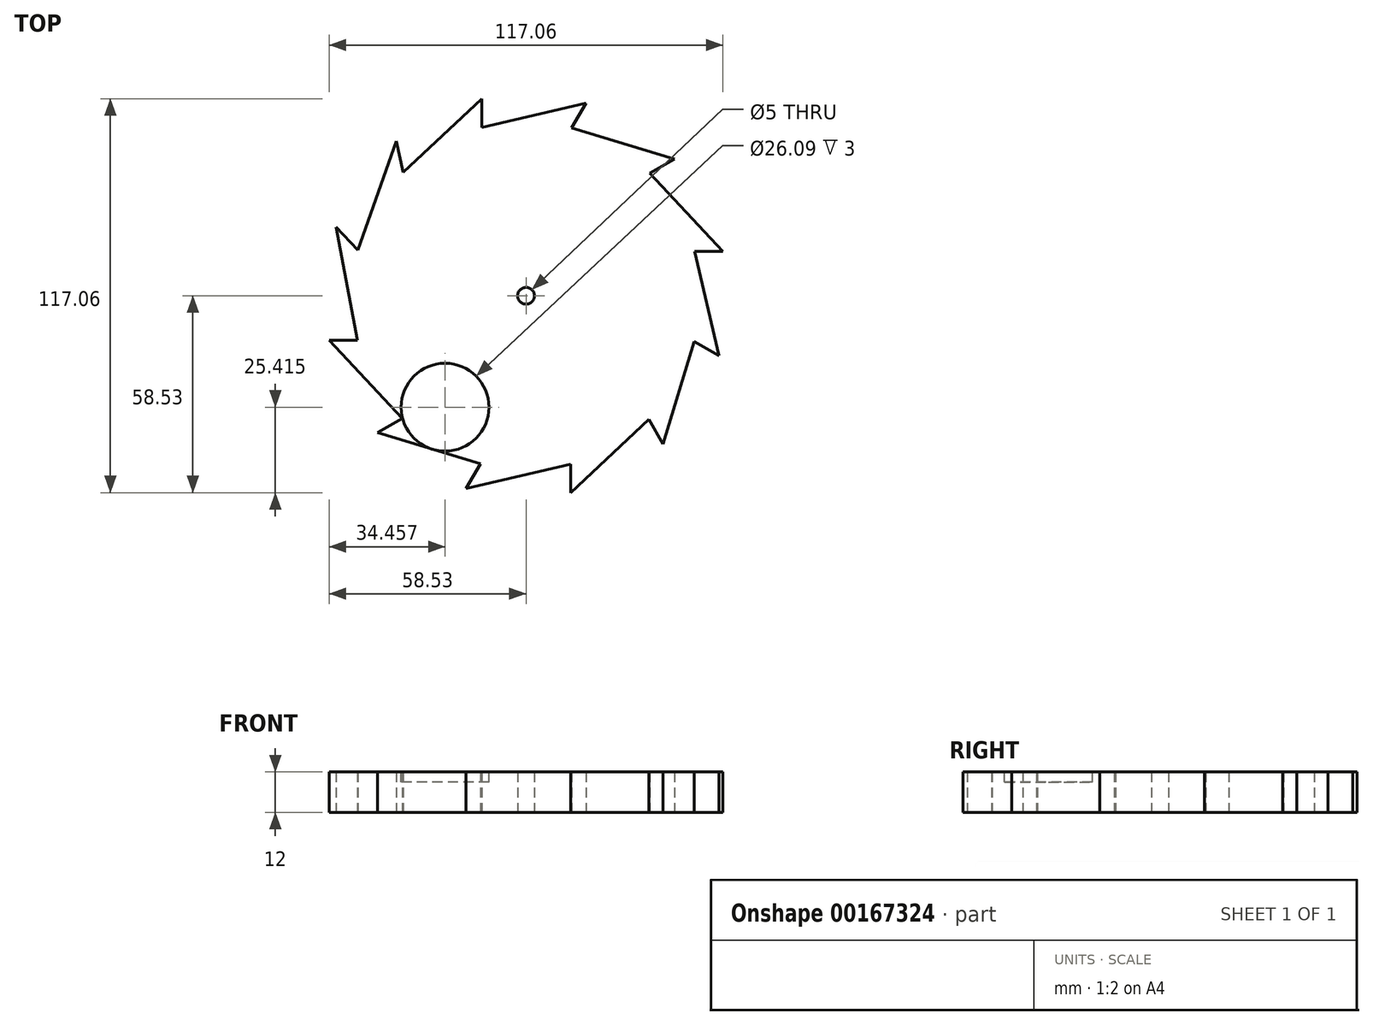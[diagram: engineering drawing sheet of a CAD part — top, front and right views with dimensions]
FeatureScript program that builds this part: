
annotation { "Feature Type Name" : "Feature", "Feature Type Description" : "" }
export const myFeature = defineFeature(function(context is Context, id is Id, definition is map)
    precondition{}
    {
        {
            var Q0;
            Q0=qCreatedBy(makeId("Top.planeOp"),FACE);
            var sketch = newSketch(context, id + "F0", { "sketchPlane" : qUnion([Q0])});
            skCircle(sketch, "E0", {"center": v(0, 0) * mm, "radius": 60 * mm});
            skCircle(sketch, "E1.cCircle", {"center": v(0, 0) * mm, "radius": 50 * mm, "construction": true});
            skLineSegment(sketch, "E1.0", {"start": v(36.47, -36.73) * mm, "end": v(13.22, -50.05) * mm});
            skLineSegment(sketch, "E1.1", {"start": v(13.22, -50.05) * mm, "end": v(-13.58, -49.95) * mm});
            skLineSegment(sketch, "E1.2", {"start": v(-13.58, -49.95) * mm, "end": v(-36.73, -36.47) * mm});
            skLineSegment(sketch, "E1.3", {"start": v(-36.73, -36.47) * mm, "end": v(-50.05, -13.22) * mm});
            skLineSegment(sketch, "E1.4", {"start": v(-50.05, -13.22) * mm, "end": v(-49.95, 13.58) * mm});
            skLineSegment(sketch, "E1.5", {"start": v(-49.95, 13.58) * mm, "end": v(-36.47, 36.73) * mm});
            skLineSegment(sketch, "E1.6", {"start": v(-36.47, 36.73) * mm, "end": v(-13.22, 50.05) * mm});
            skLineSegment(sketch, "E1.7", {"start": v(-13.22, 50.05) * mm, "end": v(13.58, 49.95) * mm});
            skLineSegment(sketch, "E1.8", {"start": v(13.58, 49.95) * mm, "end": v(36.73, 36.47) * mm});
            skLineSegment(sketch, "E1.9", {"start": v(36.73, 36.47) * mm, "end": v(50.05, 13.22) * mm});
            skLineSegment(sketch, "E1.10", {"start": v(50.05, 13.22) * mm, "end": v(49.95, -13.58) * mm});
            skLineSegment(sketch, "E1.11", {"start": v(49.95, -13.58) * mm, "end": v(36.47, -36.73) * mm});
            skPoint(sketch, "E1.0.midPoint", {"position": v(24.84, -43.4) * mm});
            skLineSegment(sketch, "E2", {"start": v(13.58, 49.95) * mm, "end": v(17.85, 57.28) * mm});
            skLineSegment(sketch, "E3", {"start": v(17.85, 57.28) * mm, "end": v(-13.22, 50.05) * mm});
            skLineSegment(sketch, "E4", {"start": v(-13.22, 50.05) * mm, "end": v(-13.22, 58.53) * mm});
            skLineSegment(sketch, "E5", {"start": v(-13.22, 58.53) * mm, "end": v(-36.47, 36.73) * mm});
            skLineSegment(sketch, "E6", {"start": v(-36.47, 36.73) * mm, "end": v(-38.61, 45.92) * mm});
            skLineSegment(sketch, "E7", {"start": v(-38.61, 45.92) * mm, "end": v(-49.95, 13.58) * mm});
            skLineSegment(sketch, "E8", {"start": v(-49.95, 13.58) * mm, "end": v(-56.4, 20.46) * mm});
            skLineSegment(sketch, "E9", {"start": v(-56.4, 20.46) * mm, "end": v(-50.05, -13.22) * mm});
            skLineSegment(sketch, "E10", {"start": v(-50.05, -13.22) * mm, "end": v(-58.53, -13.19) * mm});
            skLineSegment(sketch, "E11", {"start": v(-58.53, -13.19) * mm, "end": v(-36.73, -36.47) * mm});
            skLineSegment(sketch, "E12", {"start": v(-36.73, -36.47) * mm, "end": v(-44.1, -40.69) * mm});
            skLineSegment(sketch, "E13", {"start": v(-44.1, -40.69) * mm, "end": v(-13.58, -49.95) * mm});
            skLineSegment(sketch, "E14", {"start": v(-13.58, -49.95) * mm, "end": v(-17.85, -57.28) * mm});
            skLineSegment(sketch, "E15", {"start": v(-17.85, -57.28) * mm, "end": v(13.22, -50.05) * mm});
            skLineSegment(sketch, "E16", {"start": v(13.22, -50.05) * mm, "end": v(13.22, -58.53) * mm});
            skLineSegment(sketch, "E17", {"start": v(13.22, -58.53) * mm, "end": v(36.47, -36.73) * mm});
            skLineSegment(sketch, "E18", {"start": v(36.47, -36.73) * mm, "end": v(40.69, -44.1) * mm});
            skLineSegment(sketch, "E19", {"start": v(40.69, -44.1) * mm, "end": v(49.95, -13.58) * mm});
            skLineSegment(sketch, "E20", {"start": v(49.95, -13.58) * mm, "end": v(57.28, -17.85) * mm});
            skLineSegment(sketch, "E21", {"start": v(57.28, -17.85) * mm, "end": v(50.05, 13.22) * mm});
            skLineSegment(sketch, "E22", {"start": v(50.05, 13.22) * mm, "end": v(58.53, 13.19) * mm});
            skLineSegment(sketch, "E23", {"start": v(58.53, 13.19) * mm, "end": v(36.73, 36.47) * mm});
            skLineSegment(sketch, "E24", {"start": v(36.73, 36.47) * mm, "end": v(44.1, 40.69) * mm});
            skLineSegment(sketch, "E25", {"start": v(44.1, 40.69) * mm, "end": v(13.58, 49.95) * mm});
            skCircle(sketch, "E26", {"center": v(0, 0) * mm, "radius": 2.5 * mm});
            skSolve(sketch);
        }
        {
            var Q0;
            Q0=makeQuery(id+"F0.imprint","IMPRINT",FACE,{"disambiguationData":[TD([[makeQuery(id+"F0.imprint","IMPRINT",EDGE,{"derivedFrom":sQuery(id+"F0.wireOp",EDGE,"E1.0")}),-1.0]])]});
            var Q1;
            Q1=makeQuery(id+"F0.imprint","IMPRINT",FACE,{"disambiguationData":[TD([[makeQuery(id+"F0.imprint","IMPRINT",EDGE,{"derivedFrom":sQuery(id+"F0.wireOp",EDGE,"E1.5")}),1.0]])]});
            var Q2;
            Q2=makeQuery(id+"F0.imprint","IMPRINT",FACE,{"disambiguationData":[TD([[makeQuery(id+"F0.imprint","IMPRINT",EDGE,{"derivedFrom":sQuery(id+"F0.wireOp",EDGE,"E1.6")}),1.0]])]});
            var Q3;
            Q3=makeQuery(id+"F0.imprint","IMPRINT",FACE,{"disambiguationData":[TD([[makeQuery(id+"F0.imprint","IMPRINT",EDGE,{"derivedFrom":sQuery(id+"F0.wireOp",EDGE,"E1.3")}),1.0]])]});
            var Q4;
            Q4=makeQuery(id+"F0.imprint","IMPRINT",FACE,{"disambiguationData":[TD([[makeQuery(id+"F0.imprint","IMPRINT",EDGE,{"derivedFrom":sQuery(id+"F0.wireOp",EDGE,"E1.4")}),1.0]])]});
            var Q5;
            Q5=makeQuery(id+"F0.imprint","IMPRINT",FACE,{"disambiguationData":[TD([[makeQuery(id+"F0.imprint","IMPRINT",EDGE,{"derivedFrom":sQuery(id+"F0.wireOp",EDGE,"E1.2")}),1.0]])]});
            var Q6;
            Q6=makeQuery(id+"F0.imprint","IMPRINT",FACE,{"disambiguationData":[TD([[makeQuery(id+"F0.imprint","IMPRINT",EDGE,{"derivedFrom":sQuery(id+"F0.wireOp",EDGE,"E1.7")}),1.0]])]});
            var Q7;
            Q7=makeQuery(id+"F0.imprint","IMPRINT",FACE,{"disambiguationData":[TD([[makeQuery(id+"F0.imprint","IMPRINT",EDGE,{"derivedFrom":sQuery(id+"F0.wireOp",EDGE,"E1.8")}),1.0]])]});
            var Q8;
            Q8=makeQuery(id+"F0.imprint","IMPRINT",FACE,{"disambiguationData":[TD([[makeQuery(id+"F0.imprint","IMPRINT",EDGE,{"derivedFrom":sQuery(id+"F0.wireOp",EDGE,"E1.9")}),1.0]])]});
            var Q9;
            Q9=makeQuery(id+"F0.imprint","IMPRINT",FACE,{"disambiguationData":[TD([[makeQuery(id+"F0.imprint","IMPRINT",EDGE,{"derivedFrom":sQuery(id+"F0.wireOp",EDGE,"E1.10")}),1.0]])]});
            var Q10;
            Q10=makeQuery(id+"F0.imprint","IMPRINT",FACE,{"disambiguationData":[TD([[makeQuery(id+"F0.imprint","IMPRINT",EDGE,{"derivedFrom":sQuery(id+"F0.wireOp",EDGE,"E1.11")}),1.0]])]});
            var Q11;
            Q11=makeQuery(id+"F0.imprint","IMPRINT",FACE,{"disambiguationData":[TD([[makeQuery(id+"F0.imprint","IMPRINT",EDGE,{"derivedFrom":sQuery(id+"F0.wireOp",EDGE,"E1.0")}),1.0]])]});
            var Q12;
            Q12=makeQuery(id+"F0.imprint","IMPRINT",FACE,{"disambiguationData":[TD([[makeQuery(id+"F0.imprint","IMPRINT",EDGE,{"derivedFrom":sQuery(id+"F0.wireOp",EDGE,"E1.1")}),1.0]])]});
            extrude(context, id + "F1", {"entities" : qUnion([Q0, Q1, Q2, Q3, Q4, Q5, Q6, Q7, Q8, Q9, Q10, Q11, Q12]), "depth" : 12 * mm});
        }
        {
            var Q0;
            Q0=makeQuery(id+"F1.opExtrude","CAP_FACE",FACE,{"disambiguationData":[OSD([sQuery(id+"F0.wireOp",EDGE,"E2"),sQuery(id+"F0.wireOp",EDGE,"E3"),sQuery(id+"F0.wireOp",EDGE,"E4"),sQuery(id+"F0.wireOp",EDGE,"E5"),sQuery(id+"F0.wireOp",EDGE,"E6"),sQuery(id+"F0.wireOp",EDGE,"E7"),sQuery(id+"F0.wireOp",EDGE,"E8"),sQuery(id+"F0.wireOp",EDGE,"E9"),sQuery(id+"F0.wireOp",EDGE,"E10"),sQuery(id+"F0.wireOp",EDGE,"E11"),sQuery(id+"F0.wireOp",EDGE,"E12"),sQuery(id+"F0.wireOp",EDGE,"E13"),sQuery(id+"F0.wireOp",EDGE,"E14"),sQuery(id+"F0.wireOp",EDGE,"E15"),sQuery(id+"F0.wireOp",EDGE,"E16"),sQuery(id+"F0.wireOp",EDGE,"E17"),sQuery(id+"F0.wireOp",EDGE,"E18"),sQuery(id+"F0.wireOp",EDGE,"E19"),sQuery(id+"F0.wireOp",EDGE,"E20"),sQuery(id+"F0.wireOp",EDGE,"E21"),sQuery(id+"F0.wireOp",EDGE,"E22"),sQuery(id+"F0.wireOp",EDGE,"E23"),sQuery(id+"F0.wireOp",EDGE,"E24"),sQuery(id+"F0.wireOp",EDGE,"E25"),sQuery(id+"F0.wireOp",EDGE,"E26")])],"isStart":false});
            var sketch = newSketch(context, id + "F2", { "sketchPlane" : qUnion([Q0])});
            skCircle(sketch, "E27", {"center": v(-24.07, -33.11) * mm, "radius": 13.05 * mm});
            skSolve(sketch);
        }
        {
            var Q0;
            Q0=makeQuery(id+"F2.imprint","IMPRINT",FACE,{"disambiguationData":[TD([[makeQuery(id+"F2.imprint","IMPRINT",EDGE,{"derivedFrom":sQuery(id+"F2.wireOp",EDGE,"E27")}),1.0]])]});
            extrude(context, id + "F3", {"entities" : qUnion([Q0]), "operationType" : NewBodyOperationType.REMOVE, "oppositeDirection" : true, "depth" : 3 * mm});
        }
    });
